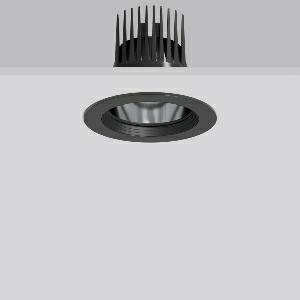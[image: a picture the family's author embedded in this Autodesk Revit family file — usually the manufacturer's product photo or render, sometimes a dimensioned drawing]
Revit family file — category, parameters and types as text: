
# Revit family: heledon_maxi_e_901763_003_76_af62
name_source: partatom
category: Lighting Fixtures
units: mm (PartAtom-declared; Revit-internal decimal feet)

## family parameters
Cut with Voids When Loaded = No
Host = Face
Light Source = No
Part Type = Normal
Room Calculation Point = No
Round Connector Dimension = Use Diameter
Shared = No

## types (1)
- HELEDON maxi E (1 x LED Modul 930, 4200 lm, 3000)
    Apparent Load = 35 VA
    Approval mark = CE
    CIE Flux Codes = 100 100 100 100 100
    Color Rendering = 90
    Color Temperature = 3000
    Default Elevation = 1800 mm
    Description = Series: HELEDON maxi
Round recessed downlight. Housing: die-cast aluminium, powder-coated. Black plastic ring and recessed LED to prevent glare from the side. Optical assembly with reflector made of MIRO-Silver with 98% total light reflection for outstanding efficiency - can be changed without tools. Best colour rendering index Ra>90. Suitable for Recessed ceiling mounting. Installation without tools thanks to spring fastening system. Including separate LED converter with connecting cable 600 mm.High quality converter without flickering and stroboscopic effect. Through-wiring box (5 pole) available as accessory. The following accessories can be mounted without use of tools: interchangeable lenses, decorative glasses, honeycomb louvre, clear and frosted diffusers, white interchangeable plastic ring. 
Colour: deep black, matt (RAL 9005)
Diameter: 162 mm
Height: 3 mm
Cut-out diameter: 152 mm
Recess height: 200 mm
Luminaire: recess height: 135 mm
Lamp: LED
Socket: without socket
Colour temperature: 3000K
Colour rendering index (CRI): 92
System power: 35 W
Rated luminous flux: 4200 lm
Luminous efficiency: 120 lm/W
Control gear: Converter, dimmable, DALI
Protection class: II
Type of protection: IP 20
    Height = 0 mm  [stored 0 ft]
    Lamp = 1 x LED Modul 930
    Lamp Light Flux = 4200 lm
    Lamp count = 1
    Length = 162 mm
    Lifetime = 50000 h
    Luminous efficacy = 120 lm/W
    Manufacturer = RZB
    ModVariant = No
    Model = 901763.003.76
    Mounting Place = Ceiling
    Mounting Type = Recessed
    Number of Poles = 1
    OnlyDefault = Yes
    Power Factor = 1
    Product Name = HELEDON maxi E
    Product group = Recessed downlights
    ProductGroupID = 402
    Protection Class = Protection class II
    Protection Degree = IP 20
    RLX_Detail_Level = 1
    RLX_Emergency_Light_Flux = 0 lm
    RLX_Emergency_Type = 0
    RLX_Emergency_Type_DB = No
    RlxData = <blob elided: 120261 chars, md5=c1cc6bd6>
    Socket = socket
    Standby Power = 0 W
    System Light Flux = 4200 lm
    System Power = 35 W
    Type Comments = Product without accessories
    Type Image = 901662.003.jpg
    URL = http://relux.com
    VarID = ---
    Voltage = 230 V
    Voltage Range = 220-240 V
    Weight = 0.00 kg
    Width = 0 mm  [stored 0 ft]

note: [stored X ft] marks values corroborated as IEEE doubles in the binary element streams (Revit-internal decimal feet)

## geometry (parser evidence)
native form markers: Blend x4, Sweep x12
no freeform markers — native parametric forms only
